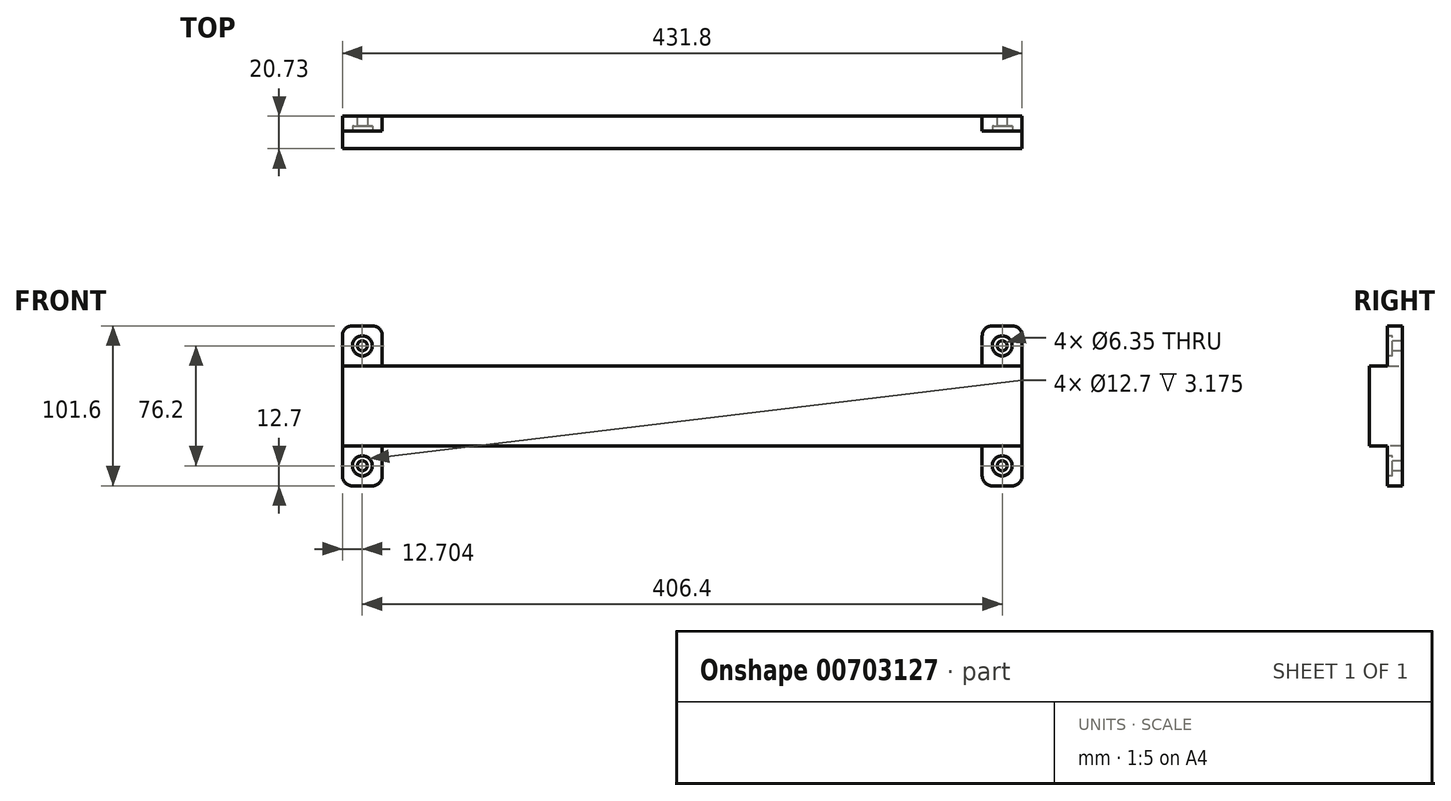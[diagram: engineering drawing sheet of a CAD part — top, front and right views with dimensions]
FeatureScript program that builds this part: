
annotation { "Feature Type Name" : "Feature", "Feature Type Description" : "" }
export const myFeature = defineFeature(function(context is Context, id is Id, definition is map)
    precondition{}
    {
        {
            var Q0;
            Q0=qCreatedBy(makeId("Front.planeOp"),FACE);
            var sketch = newSketch(context, id + "F0", { "sketchPlane" : qUnion([Q0])});
            skLineSegment(sketch, "E0.bottom", {"start": v(-195.33, -62.84) * mm, "end": v(236.47, -62.84) * mm});
            skLineSegment(sketch, "E0.top", {"start": v(-195.33, -12.04) * mm, "end": v(236.47, -12.04) * mm});
            skLineSegment(sketch, "E0.left", {"start": v(-195.33, -62.84) * mm, "end": v(-195.33, -12.04) * mm});
            skLineSegment(sketch, "E0.right", {"start": v(236.47, -62.84) * mm, "end": v(236.47, -12.04) * mm});
            skSolve(sketch);
        }
        {
            var Q0;
            Q0=makeQuery(id+"F0.imprint","IMPRINT",FACE,{"disambiguationData":[TD([[makeQuery(id+"F0.imprint","IMPRINT",EDGE,{"derivedFrom":sQuery(id+"F0.wireOp",EDGE,"E0.bottom")}),1.0]])]});
            extrude(context, id + "F1", {"entities" : qUnion([Q0]), "depth" : 20.73 * mm, "offsetDistance" : 25.4 * mm});
        }
        {
            var Q0;
            Q0=makeQuery(id+"F1.opExtrude","SWEPT_FACE",FACE,{"disambiguationData":[OSD([sQuery(id+"F0.wireOp",EDGE,"E0.bottom")])]});
            var sketch = newSketch(context, id + "F2", { "sketchPlane" : qUnion([Q0])});
            skLineSegment(sketch, "E1.bottom", {"start": v(-195.33, 0) * mm, "end": v(-169.93, 0) * mm});
            skLineSegment(sketch, "E1.top", {"start": v(-195.33, 9.53) * mm, "end": v(-169.93, 9.53) * mm});
            skLineSegment(sketch, "E1.left", {"start": v(-195.33, 0) * mm, "end": v(-195.33, 9.53) * mm});
            skLineSegment(sketch, "E1.right", {"start": v(-169.93, 0) * mm, "end": v(-169.93, 9.53) * mm});
            skLineSegment(sketch, "E2.bottom", {"start": v(236.47, 0) * mm, "end": v(211.07, 0) * mm});
            skLineSegment(sketch, "E2.top", {"start": v(236.47, 9.52) * mm, "end": v(211.07, 9.52) * mm});
            skLineSegment(sketch, "E2.left", {"start": v(236.47, 0) * mm, "end": v(236.47, 9.52) * mm});
            skLineSegment(sketch, "E2.right", {"start": v(211.07, 0) * mm, "end": v(211.07, 9.52) * mm});
            skSolve(sketch);
        }
        {
            var Q0;
            Q0=qSketchRegion(id+"F2",true);
            extrude(context, id + "F3", {"entities" : qUnion([Q0]), "operationType" : NewBodyOperationType.ADD, "depth" : 25.4 * mm, "offsetDistance" : 25.4 * mm});
        }
        {
            var Q0;
            Q0=makeQuery(id+"F1.opExtrude","SWEPT_FACE",FACE,{"disambiguationData":[OSD([sQuery(id+"F0.wireOp",EDGE,"E0.top")])]});
            var sketch = newSketch(context, id + "F4", { "sketchPlane" : qUnion([Q0])});
            skPoint(sketch, "E3.0", {"position": v(-182.63, -9.53) * mm});
            skLineSegment(sketch, "E4.0", {"start": v(-195.33, 0) * mm, "end": v(-169.93, 0) * mm});
            skLineSegment(sketch, "E5.0", {"start": v(-195.33, -9.53) * mm, "end": v(-195.33, 0) * mm});
            skLineSegment(sketch, "E6.0", {"start": v(-169.93, 0) * mm, "end": v(-169.93, -9.53) * mm});
            skLineSegment(sketch, "E7.0.0", {"start": v(211.07, -9.52) * mm, "end": v(211.07, 0) * mm});
            skLineSegment(sketch, "E7.0.1", {"start": v(211.07, 0) * mm, "end": v(236.47, 0) * mm});
            skLineSegment(sketch, "E7.0.2", {"start": v(236.47, 0) * mm, "end": v(236.47, -9.52) * mm});
            skLineSegment(sketch, "E7.0.3", {"start": v(236.47, -9.52) * mm, "end": v(211.07, -9.52) * mm});
            skLineSegment(sketch, "E8.0", {"start": v(-195.33, -9.53) * mm, "end": v(-169.93, -9.53) * mm});
            skSolve(sketch);
        }
        {
            var Q0;
            Q0=qSketchRegion(id+"F4",true);
            extrude(context, id + "F5", {"entities" : qUnion([Q0]), "operationType" : NewBodyOperationType.ADD, "depth" : 25.4 * mm, "offsetDistance" : 25.4 * mm});
        }
        {
            var Q0;
            Q0=makeQuery(id+"F3.opExtrude","CAP_EDGE",EDGE,{"disambiguationData":[OSD([sQuery(id+"F2.wireOp",EDGE,"E2.left")])],"isStart":false});
            var Q1;
            Q1=makeQuery(id+"F3.opExtrude","CAP_EDGE",EDGE,{"disambiguationData":[OSD([sQuery(id+"F2.wireOp",EDGE,"E2.right")])],"isStart":false});
            var Q2;
            Q2=makeQuery(id+"F5.opExtrude","CAP_EDGE",EDGE,{"disambiguationData":[OSD([sQuery(id+"F4.wireOp",EDGE,"E7.0.2")])],"isStart":false});
            var Q3;
            Q3=makeQuery(id+"F5.opExtrude","CAP_EDGE",EDGE,{"disambiguationData":[OSD([sQuery(id+"F4.wireOp",EDGE,"E7.0.0")])],"isStart":false});
            var Q4;
            Q4=makeQuery(id+"F5.opExtrude","CAP_EDGE",EDGE,{"disambiguationData":[OSD([sQuery(id+"F4.wireOp",EDGE,"E6.0")])],"isStart":false});
            var Q5;
            Q5=makeQuery(id+"F5.opExtrude","CAP_EDGE",EDGE,{"disambiguationData":[OSD([sQuery(id+"F4.wireOp",EDGE,"E5.0")])],"isStart":false});
            var Q6;
            Q6=makeQuery(id+"F3.opExtrude","CAP_EDGE",EDGE,{"disambiguationData":[OSD([sQuery(id+"F2.wireOp",EDGE,"E1.left")])],"isStart":false});
            var Q7;
            Q7=makeQuery(id+"F3.opExtrude","CAP_EDGE",EDGE,{"disambiguationData":[OSD([sQuery(id+"F2.wireOp",EDGE,"E1.right")])],"isStart":false});
            fillet(context, id + "F6", {"entities" : qUnion([Q0, Q1, Q2, Q3, Q4, Q5, Q6, Q7]), "radius" : 6.35 * mm, "tangentPropagation" : true, "allowEdgeOverflow" : false});
        }
        {
            var Q0;
            Q0=makeQuery(id+"F3.opExtrude","SWEPT_FACE",FACE,{"disambiguationData":[OSD([sQuery(id+"F2.wireOp",EDGE,"E1.top")])]});
            var sketch = newSketch(context, id + "F7", { "sketchPlane" : qUnion([Q0])});
            skPoint(sketch, "E9", {"position": v(-182.63, -75.54) * mm});
            skPoint(sketch, "E9.positionSnap0", {"position": v(-169.93, -75.54) * mm});
            skPoint(sketch, "E9.positionSnap1", {"position": v(-182.63, -62.84) * mm});
            skPoint(sketch, "E10", {"position": v(-182.63, 0.66) * mm});
            skPoint(sketch, "E11", {"position": v(223.77, 0.66) * mm});
            skPoint(sketch, "E12", {"position": v(223.77, -75.54) * mm});
            skSolve(sketch);
        }
        {
            var Q0;
            Q0=sQuery(id+"F7.wireOp",VERTEX,"E10");
            var Q1;
            Q1=sQuery(id+"F7.wireOp",VERTEX,"E9");
            var Q2;
            Q2=sQuery(id+"F7.wireOp",VERTEX,"E11");
            var Q3;
            Q3=sQuery(id+"F7.wireOp",VERTEX,"E12");
            var Q4;
            Q4=makeQuery(id+"F1.opExtrude","SWEPT_BODY",BODY,{"disambiguationData":[OSD([sQuery(id+"F0.wireOp",EDGE,"E0.bottom"),sQuery(id+"F0.wireOp",EDGE,"E0.top"),sQuery(id+"F0.wireOp",EDGE,"E0.left"),sQuery(id+"F0.wireOp",EDGE,"E0.right")])]});
            hole(context, id + "F8", {"style" : HoleStyle.C_BORE, "endStyle" : HoleEndStyle.THROUGH, "holeDiameter" : 6.35 * mm, "cBoreDiameter" : 12.7 * mm, "cBoreDepth" : 3.17 * mm, "majorDiameter" : 6.35 * mm, "isTappedThrough" : true, "tappedDepth" : 12.7 * mm, "tapClearance" : 3, "locations" : qUnion([Q0, Q1, Q2, Q3]), "scope" : qUnion([Q4])});
        }
    });
